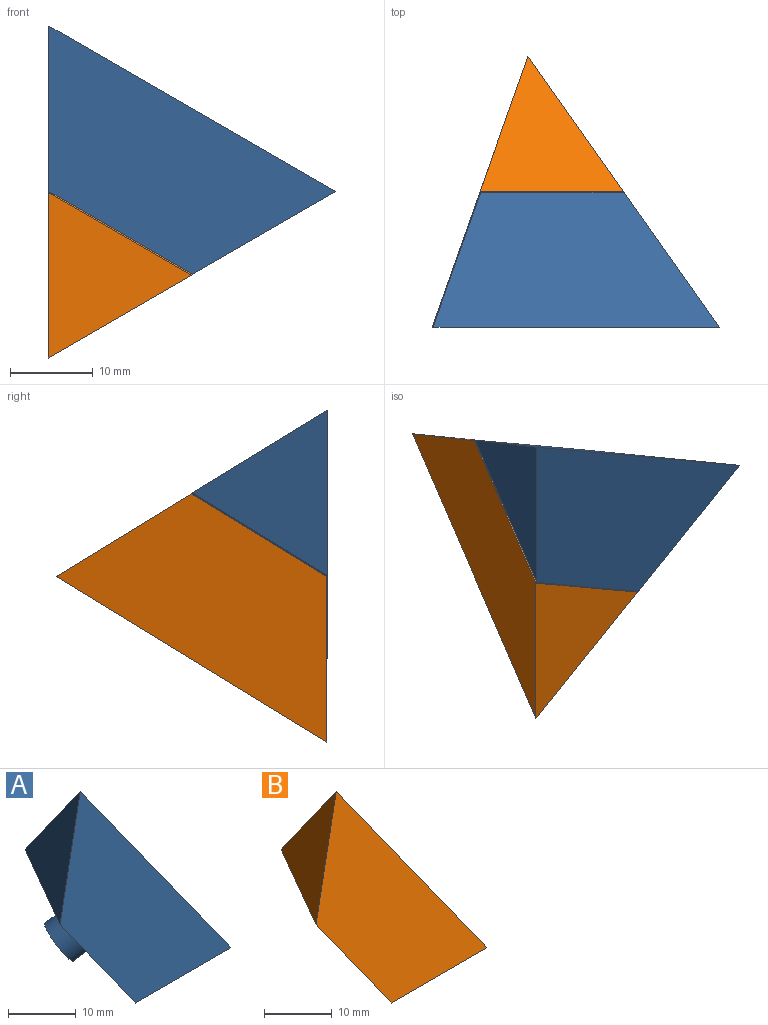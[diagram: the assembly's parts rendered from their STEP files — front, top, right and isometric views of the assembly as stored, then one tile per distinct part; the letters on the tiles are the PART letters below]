
ASSEMBLY  parts=2 mates=1
PART A: 7 faces, bbox 30x23.1x32.7 mm
  f0: plane 32.66x23.09mm, normal (0.82,0.47,0.33), area 519.6mm2, adj f1,f2,f3,f4
  f1: plane 20x17.32mm, normal (0,0,-1), area 173.2mm2, adj f0,f3,f4
  f2: plane 17.32x16.33mm, normal (-0.82,0.47,0.33), area 173.2mm2, adj f0,f3,f4
  f3: plane 32.66x30mm, normal (0,-0.94,0.33), area 519.6mm2, adj f0,f1,f2,f4
  f4: plane 23.09x20mm, normal (-0.71,0.41,-0.58), area 361.5mm2, adj f0,f1,f2,f3,f5
  f5: cylinder r=3.5mm len=8.03mm, axis (0.71,-0.41,0.58), area 88mm2, adj f4,f6
  f6: plane 6.39x5.72mm, normal (-0.71,0.41,-0.58), area 38.5mm2, adj f5
PART B: 7 faces, bbox 30x23.1x32.7 mm
  f0: plane 32.66x23.09mm, normal (0.82,0.47,0.33), area 519.6mm2, adj f1,f2,f3,f4
  f1: plane 20x17.32mm, normal (0,0,-1), area 173.2mm2, adj f0,f3,f4
  f2: plane 17.32x16.33mm, normal (-0.82,0.47,0.33), area 173.2mm2, adj f0,f3,f4
  f3: plane 32.66x30mm, normal (0,-0.94,0.33), area 519.6mm2, adj f0,f1,f2,f4
  f4: plane 23.09x20mm, normal (-0.71,0.41,-0.58), area 359.8mm2, adj f0,f1,f2,f3,f5
  f5: cylinder r=3.58mm len=8.26mm, axis (-0.71,0.41,-0.58), area 94.3mm2, adj f4,f6
  f6: plane 6.53x5.84mm, normal (-0.71,0.41,-0.58), area 40.2mm2, adj f5
PLACE A rot(axis=(0.53,-0.83,0.14),35.6deg) t=(0,0,-30)mm
PLACE B rot(axis=(0.8,0.51,-0.3),178.4deg) t=(-0.07,0.1,9.88)mm
MATE slider B.f5 <-> A.f5  axis (0.41,-0.58,0.71) through (9.76,10.69,-13.09)mm
